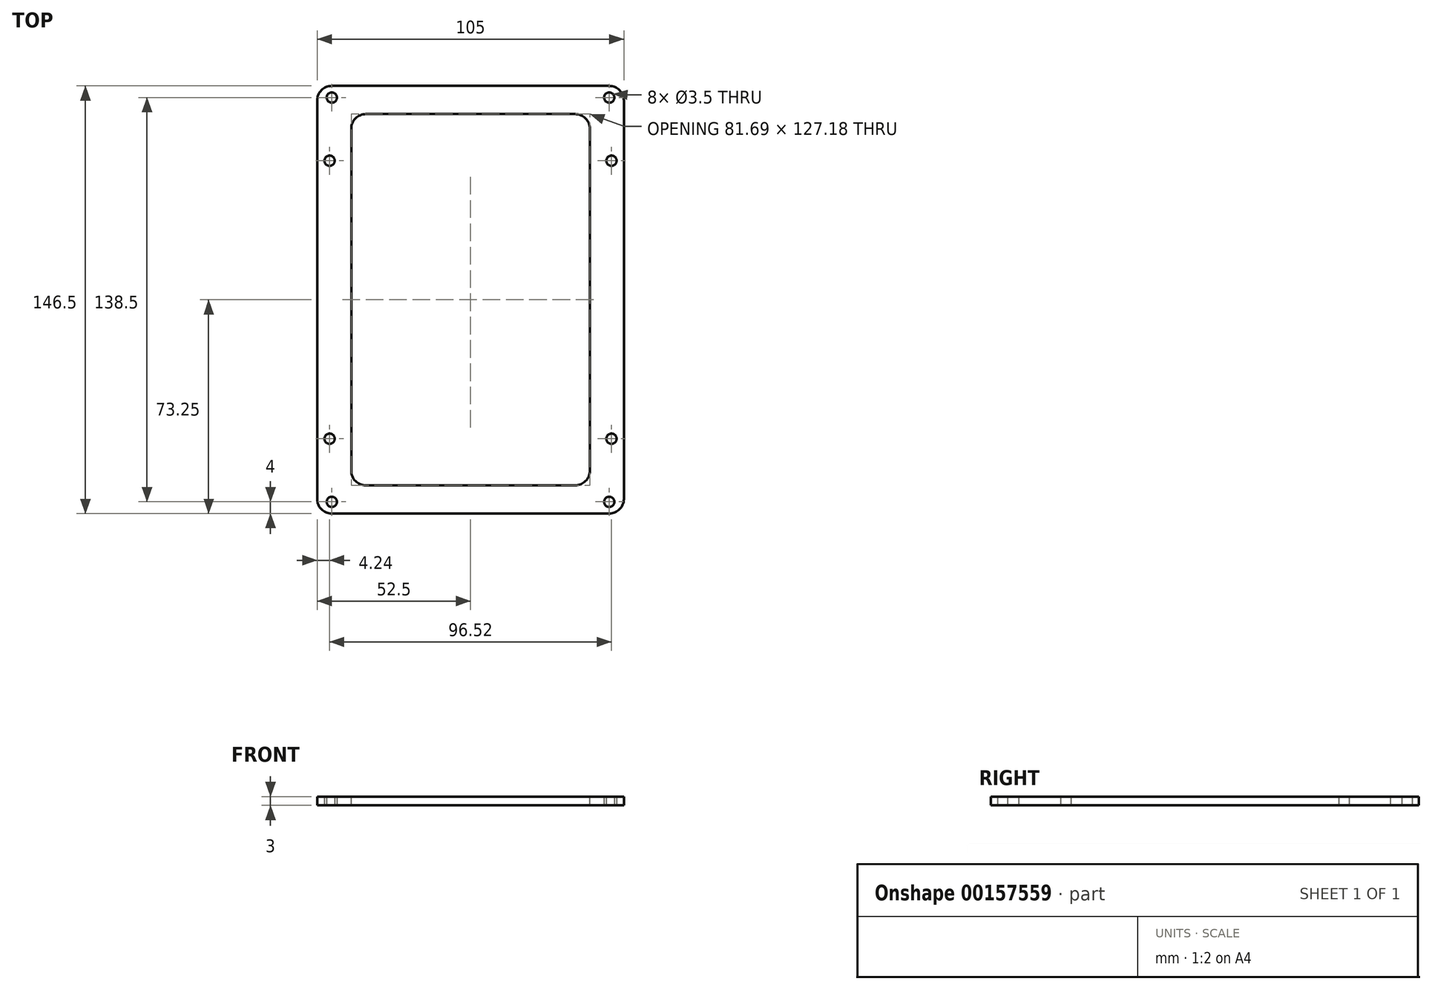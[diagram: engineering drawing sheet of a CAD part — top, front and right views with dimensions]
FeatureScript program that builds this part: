
annotation { "Feature Type Name" : "Feature", "Feature Type Description" : "" }
export const myFeature = defineFeature(function(context is Context, id is Id, definition is map)
    precondition{}
    {
        {
            var Q0;
            Q0=qCreatedBy(makeId("Top.planeOp"),FACE);
            var sketch = newSketch(context, id + "F0", { "sketchPlane" : qUnion([Q0])});
            skLineSegment(sketch, "E0.bottom", {"start": v(52.07, 51.44) * mm, "end": v(-52.07, 51.44) * mm, "construction": true});
            skLineSegment(sketch, "E0.top", {"start": v(52.07, -51.43) * mm, "end": v(-52.07, -51.43) * mm, "construction": true});
            skLineSegment(sketch, "E0.left", {"start": v(52.07, 51.44) * mm, "end": v(52.07, -51.43) * mm, "construction": true});
            skLineSegment(sketch, "E0.right", {"start": v(-52.07, 51.44) * mm, "end": v(-52.07, -51.43) * mm, "construction": true});
            skPoint(sketch, "E0.middle", {"position": v(0, 0) * mm});
            skLineSegment(sketch, "E1.bottom", {"start": v(48.26, 47.62) * mm, "end": v(-48.26, 47.62) * mm, "construction": true});
            skLineSegment(sketch, "E1.top", {"start": v(48.26, -47.62) * mm, "end": v(-48.26, -47.62) * mm, "construction": true});
            skLineSegment(sketch, "E1.left", {"start": v(48.26, 47.62) * mm, "end": v(48.26, -47.62) * mm, "construction": true});
            skLineSegment(sketch, "E1.right", {"start": v(-48.26, 47.62) * mm, "end": v(-48.26, -47.62) * mm, "construction": true});
            skCircle(sketch, "E2", {"center": v(-48.26, 47.62) * mm, "radius": 1.75 * mm});
            skCircle(sketch, "E3", {"center": v(-48.26, -47.62) * mm, "radius": 1.75 * mm});
            skCircle(sketch, "E4", {"center": v(48.26, -47.62) * mm, "radius": 1.75 * mm});
            skCircle(sketch, "E5", {"center": v(48.26, 47.62) * mm, "radius": 1.75 * mm});
            skLineSegment(sketch, "E6.bottom", {"start": v(52.5, 73.25) * mm, "end": v(-52.5, 73.25) * mm});
            skLineSegment(sketch, "E6.top", {"start": v(52.5, -73.25) * mm, "end": v(-52.5, -73.25) * mm});
            skLineSegment(sketch, "E6.left", {"start": v(52.5, 73.25) * mm, "end": v(52.5, -73.25) * mm});
            skLineSegment(sketch, "E6.right", {"start": v(-52.5, 73.25) * mm, "end": v(-52.5, -73.25) * mm});
            skLineSegment(sketch, "E7.bottom", {"start": v(47.5, 69.25) * mm, "end": v(-47.5, 69.25) * mm, "construction": true});
            skLineSegment(sketch, "E7.top", {"start": v(47.5, -69.25) * mm, "end": v(-47.5, -69.25) * mm, "construction": true});
            skLineSegment(sketch, "E7.left", {"start": v(47.5, 69.25) * mm, "end": v(47.5, -69.25) * mm, "construction": true});
            skLineSegment(sketch, "E7.right", {"start": v(-47.5, 69.25) * mm, "end": v(-47.5, -69.25) * mm, "construction": true});
            skCircle(sketch, "E8", {"center": v(-47.5, 69.25) * mm, "radius": 1.75 * mm});
            skCircle(sketch, "E9", {"center": v(47.5, 69.25) * mm, "radius": 1.75 * mm});
            skCircle(sketch, "E10", {"center": v(47.5, -69.25) * mm, "radius": 1.75 * mm});
            skCircle(sketch, "E11", {"center": v(-47.5, -69.25) * mm, "radius": 1.75 * mm});
            skSolve(sketch);
        }
        {
            var Q0;
            Q0=makeQuery(id+"F0.imprint","IMPRINT",FACE,{"disambiguationData":[TD([[makeQuery(id+"F0.imprint","IMPRINT",EDGE,{"derivedFrom":sQuery(id+"F0.wireOp",EDGE,"E2")}),-1.0]])]});
            extrude(context, id + "F1", {"entities" : qUnion([Q0]), "depth" : 3 * mm});
        }
        {
            var Q0;
            Q0=makeQuery(id+"F1.opExtrude","CAP_FACE",FACE,{"disambiguationData":[OSD([sQuery(id+"F0.wireOp",EDGE,"E2"),sQuery(id+"F0.wireOp",EDGE,"E3"),sQuery(id+"F0.wireOp",EDGE,"E4"),sQuery(id+"F0.wireOp",EDGE,"E5"),sQuery(id+"F0.wireOp",EDGE,"E6.bottom"),sQuery(id+"F0.wireOp",EDGE,"E6.top"),sQuery(id+"F0.wireOp",EDGE,"E6.left"),sQuery(id+"F0.wireOp",EDGE,"E6.right"),sQuery(id+"F0.wireOp",EDGE,"E8"),sQuery(id+"F0.wireOp",EDGE,"E9"),sQuery(id+"F0.wireOp",EDGE,"E10"),sQuery(id+"F0.wireOp",EDGE,"E11")])],"isStart":false});
            var sketch = newSketch(context, id + "F2", { "sketchPlane" : qUnion([Q0])});
            skLineSegment(sketch, "E12.bottom", {"start": v(40.85, 63.6) * mm, "end": v(-40.85, 63.6) * mm});
            skLineSegment(sketch, "E12.top", {"start": v(40.85, -63.6) * mm, "end": v(-40.85, -63.6) * mm});
            skLineSegment(sketch, "E12.left", {"start": v(40.85, 63.6) * mm, "end": v(40.85, -63.6) * mm});
            skLineSegment(sketch, "E12.right", {"start": v(-40.85, 63.6) * mm, "end": v(-40.85, -63.6) * mm});
            skPoint(sketch, "E12.middle", {"position": v(0, 0) * mm});
            skSolve(sketch);
        }
        {
            var Q0;
            Q0=makeQuery(id+"F2.imprint","IMPRINT",FACE,{"disambiguationData":[TD([[makeQuery(id+"F2.imprint","IMPRINT",EDGE,{"derivedFrom":sQuery(id+"F2.wireOp",EDGE,"E12.bottom")}),1.0]])]});
            extrude(context, id + "F3", {"entities" : qUnion([Q0]), "operationType" : NewBodyOperationType.REMOVE, "oppositeDirection" : true, "depth" : 25 * mm});
        }
        {
            var Q0;
            Q0=makeQuery(id+"F1.opExtrude","SWEPT_EDGE",EDGE,{"disambiguationData":[OSD([sQuery(id+"F0.wireOp",EDGE,"E6.bottom"),sQuery(id+"F0.wireOp",EDGE,"E6.right")])]});
            var Q1;
            Q1=makeQuery(id+"F1.opExtrude","SWEPT_EDGE",EDGE,{"disambiguationData":[OSD([sQuery(id+"F0.wireOp",EDGE,"E6.top"),sQuery(id+"F0.wireOp",EDGE,"E6.right")])]});
            var Q2;
            Q2=makeQuery(id+"F1.opExtrude","SWEPT_EDGE",EDGE,{"disambiguationData":[OSD([sQuery(id+"F0.wireOp",EDGE,"E6.top"),sQuery(id+"F0.wireOp",EDGE,"E6.left")])]});
            var Q3;
            Q3=makeQuery(id+"F3.boolean.opBoolean","COPY",EDGE,{"derivedFrom":makeQuery(id+"F3.opExtrude","SWEPT_EDGE",EDGE,{"disambiguationData":[OSD([sQuery(id+"F2.wireOp",EDGE,"E12.bottom"),sQuery(id+"F2.wireOp",EDGE,"E12.right")])]})});
            var Q4;
            Q4=makeQuery(id+"F1.opExtrude","SWEPT_EDGE",EDGE,{"disambiguationData":[OSD([sQuery(id+"F0.wireOp",EDGE,"E6.bottom"),sQuery(id+"F0.wireOp",EDGE,"E6.left")])]});
            var Q5;
            Q5=makeQuery(id+"F3.boolean.opBoolean","COPY",EDGE,{"derivedFrom":makeQuery(id+"F3.opExtrude","SWEPT_EDGE",EDGE,{"disambiguationData":[OSD([sQuery(id+"F2.wireOp",EDGE,"E12.bottom"),sQuery(id+"F2.wireOp",EDGE,"E12.left")])]})});
            var Q6;
            Q6=makeQuery(id+"F3.boolean.opBoolean","COPY",EDGE,{"derivedFrom":makeQuery(id+"F3.opExtrude","SWEPT_EDGE",EDGE,{"disambiguationData":[OSD([sQuery(id+"F2.wireOp",EDGE,"E12.top"),sQuery(id+"F2.wireOp",EDGE,"E12.left")])]})});
            var Q7;
            Q7=makeQuery(id+"F3.boolean.opBoolean","COPY",EDGE,{"derivedFrom":makeQuery(id+"F3.opExtrude","SWEPT_EDGE",EDGE,{"disambiguationData":[OSD([sQuery(id+"F2.wireOp",EDGE,"E12.top"),sQuery(id+"F2.wireOp",EDGE,"E12.right")])]})});
            fillet(context, id + "F4", {"entities" : qUnion([Q0, Q1, Q2, Q3, Q4, Q5, Q6, Q7]), "radius" : 5 * mm, "tangentPropagation" : true, "allowEdgeOverflow" : false});
        }
    });
